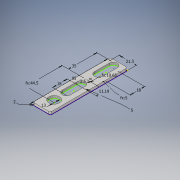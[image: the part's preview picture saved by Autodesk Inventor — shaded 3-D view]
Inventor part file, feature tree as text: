
AUTODESK INVENTOR PART (.ipt)
format: ipt  version: 2019 (Build 230136000, 136)  size: 135,680 bytes
history: native  units: mm
features: extrude x2, sketch x1
ambient origin geometry x8: Origin, YZ Plane, XZ Plane, XY Plane, X Axis, Y Axis, Z Axis, Center Point
bodies: Solid1 (feature_tree)
feature tree (3):
  sketch  "Sketch1"  dims[d0=21.3mm d1=95.0mm d2=2.5mm d3=35.0mm d6=10.65mm d8=2.0mm d9=13.0mm d10=44.5mm d11=3.0mm d12=0.0mm d13=18.0mm d14=5.0mm d15=10.0mm d16=0.0mm d17=11.189852mm d18=18.0mm d19=5.0mm]
  extrude  "Extrusion1"  Depth=95.0mm
  extrude  "Extrusion2"  Depth=5.0mm
